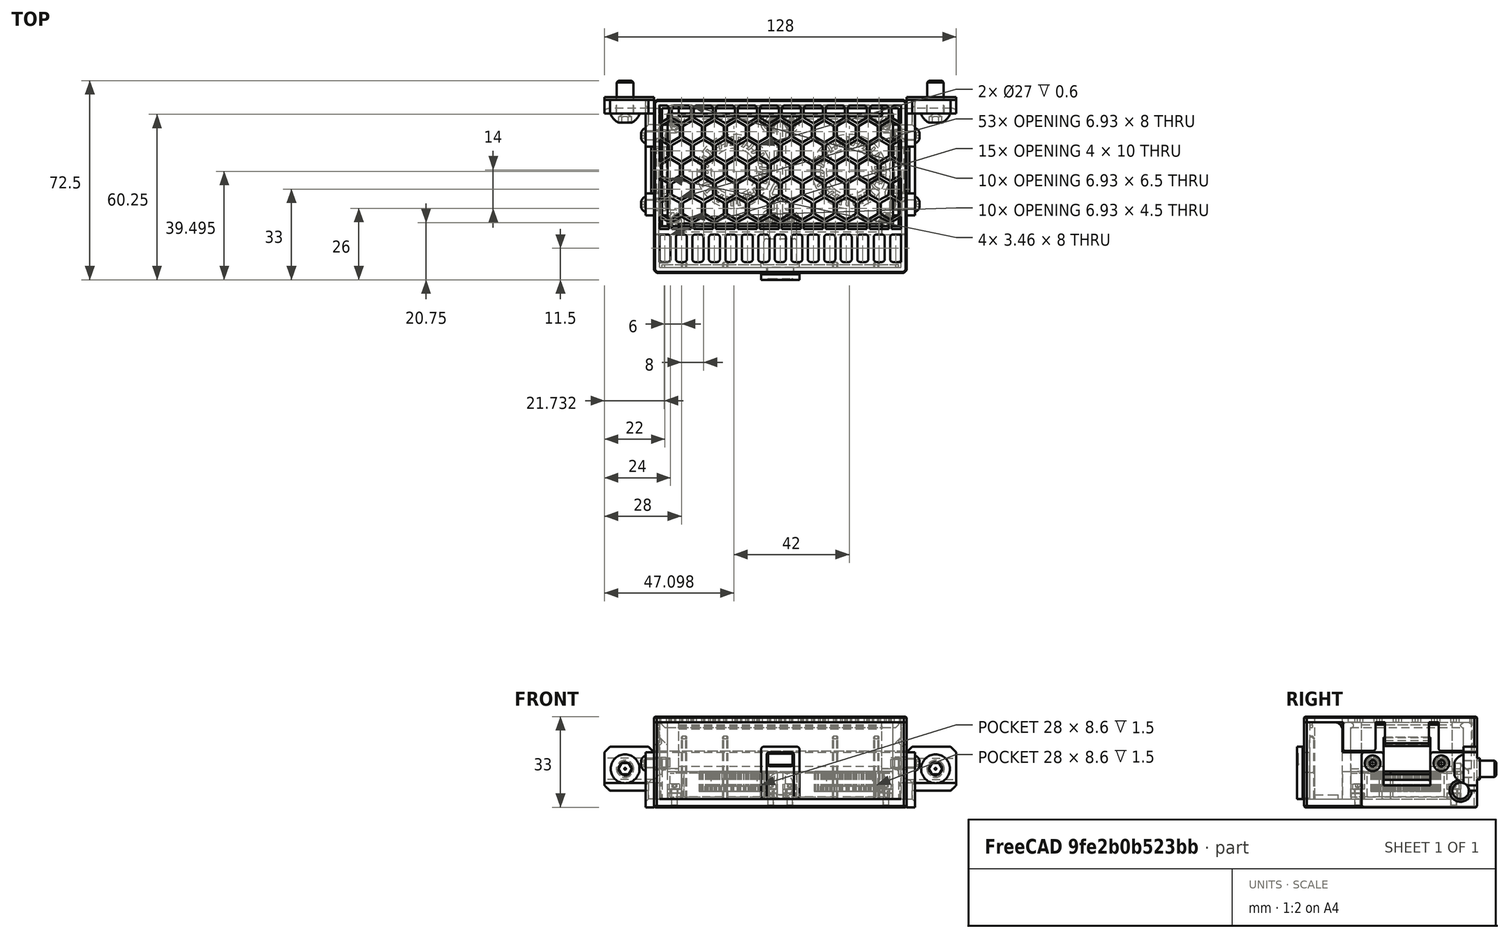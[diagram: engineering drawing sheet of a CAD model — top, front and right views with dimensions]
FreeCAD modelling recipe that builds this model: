
FCSTD DOCUMENT  (FreeCAD 0.19R24291 (Git))
Label: air-filter-assembly
License: Other
LicenseURL: GPL3
objects: Part::FeaturePython×18, Part::Feature×7, Part::Box×2, Spreadsheet::Sheet×2, PartDesign::CoordinateSystem×1, App::Part×1
note: 28 computed .brp shape members not serialized (recipe doc carries the construction recipe); baked Part::Feature solids carry a one-line shape summary decoded from their .brp

FEATURE [Part::Box] Box  label="hepa-filter"
  AttacherType = Attacher::AttachEngine3D
  Height = 16
  Length = 82
  Placement = pos=(-41,-20.5,13) rot=(0,0,1;0rad)
  Width = 41
FEATURE [Part::Box] Box001  label="active-carbon-foam"
  AttacherType = Attacher::AttachEngine3D
  Height = 28
  Length = 88
  Placement = pos=(-44,-33.5,3) rot=(0,0,1;0rad)
  Width = 10
FEATURE [Part::Feature] Part__Mirroring001001  label="air-filter-mounter-left"
  shape: bbox 18 x 43 x 22 mm, 33 faces (baked)
FEATURE [Part::Feature] Chamfer010015011016002001  label="air-filter-mounter-right"
  shape: bbox 18 x 43 x 22 mm, 33 faces (baked)
FEATURE [Part::Feature] Chamfer010015011013001001  label="air-filter-front-cover"
  shape: bbox 92 x 63 x 12.5 mm, 653 faces (baked)
FEATURE [Part::Feature] Chamfer010015011010001001  label="air-filter-body"
  shape: bbox 92 x 63 x 31 mm, 194 faces (baked)
FEATURE [Part::Feature] Cut019003010005001002001001  label="air-filter-eject-level"
  shape: bbox 14 x 15 x 19 mm, 37 faces (baked)
FEATURE [Part::Feature] Fusion036012039009  label="4010-fan001"
  Placement = pos=(-21.1,-20.5,3) rot=(-1,0,0;1.5708rad)
  shape: bbox 40 x 40 x 10 mm, 256 faces, 2 solids (baked)
FEATURE [Part::Feature] Fusion001021004009015013015  label="4010-fan002"
  Placement = pos=(20.9,-20.5,3) rot=(-1,0,0;1.5708rad)
  shape: bbox 40 x 40 x 10 mm, 256 faces, 2 solids (baked)
FEATURE [Part::FeaturePython] Screw  label="M3x6-Screw"  # Fasteners workbench fastener (typed FeaturePython)
  Placement = pos=(-49,12.5,16) rot=(0,-1,0;1.5708rad)
  baseObject = -> Part__Mirroring001001 [Edge89]
  diameter = 1
  invert = true
  length = 0
  lengthCustom = 6
  matchOuter = true
  offset = 0
  thread = false
  type = 39
FEATURE [Part::FeaturePython] Screw001  label="M3x6-Screw004"  # Fasteners workbench fastener (typed FeaturePython)
  Placement = pos=(-49,-12.5,16) rot=(0,-1,0;1.5708rad)
  baseObject = -> Part__Mirroring001001 [Edge91]
  diameter = 1
  invert = true
  length = 0
  lengthCustom = 6
  matchOuter = true
  offset = 0
  thread = false
  type = 39
FEATURE [Part::FeaturePython] Screw002  label="M3x6-Screw002"  # Fasteners workbench fastener (typed FeaturePython)
  Placement = pos=(49,12.5,16) rot=(0,1,0;1.5708rad)
  baseObject = -> Chamfer010015011016002001 [Edge89]
  diameter = 1
  invert = false
  length = 0
  lengthCustom = 6
  matchOuter = true
  offset = 0
  thread = false
  type = 39
FEATURE [Part::FeaturePython] Screw003  label="M3x6-Screw003"  # Fasteners workbench fastener (typed FeaturePython)
  Placement = pos=(49,-12.5,16) rot=(0,1,0;1.5708rad)
  baseObject = -> Chamfer010015011016002001 [Edge91]
  diameter = 1
  invert = false
  length = 0
  lengthCustom = 6
  matchOuter = true
  offset = 0
  thread = false
  type = 39
FEATURE [Part::FeaturePython] Screw004  label="M6x12-Screw"  # Fasteners workbench fastener (typed FeaturePython)
  Placement = pos=(-56.5,20.5,14) rot=(1,0,0;1.5708rad)
  baseObject = -> Part__Mirroring001001 [Edge57]
  diameter = 4
  invert = false
  length = 1
  lengthCustom = 12
  matchOuter = true
  offset = 0
  thread = false
  type = 39
FEATURE [Part::FeaturePython] Screw005  label="M6x12-Screw001"  # Fasteners workbench fastener (typed FeaturePython)
  Placement = pos=(56.5,20.5,14) rot=(1,0,0;1.5708rad)
  baseObject = -> Chamfer010015011016002001 [Edge40]
  diameter = 4
  invert = true
  length = 1
  lengthCustom = 12
  matchOuter = true
  offset = 0
  thread = false
  type = 39
FEATURE [Part::FeaturePython] HeatSet  label="M3x3-HeatSet003"  # WARN: FeaturePython — macro-defined, semantics opaque (R4)
  Placement = pos=(-46,12.5,16) rot=(0,-1,0;1.5708rad)
  baseObject = -> Chamfer010015011010001001 [Edge17]
  diameter = 2
  invert = true
  offset = 0
FEATURE [Part::FeaturePython] HeatSet001  label="M3x3-HeatSet001"  # WARN: FeaturePython — macro-defined, semantics opaque (R4)
  Placement = pos=(-46,-12.5,16) rot=(0,-1,0;1.5708rad)
  baseObject = -> Chamfer010015011010001001 [Edge16]
  diameter = 2
  invert = true
  offset = 0
FEATURE [Part::FeaturePython] HeatSet002  label="M3x3-HeatSet"  # WARN: FeaturePython — macro-defined, semantics opaque (R4)
  Placement = pos=(46,12.5,16) rot=(0,1,0;1.5708rad)
  baseObject = -> Chamfer010015011010001001 [Edge138]
  diameter = 2
  invert = false
  offset = 0
FEATURE [Part::FeaturePython] HeatSet003  label="M3x3-HeatSet002"  # WARN: FeaturePython — macro-defined, semantics opaque (R4)
  Placement = pos=(46,-12.5,16) rot=(0,1,0;1.5708rad)
  baseObject = -> Chamfer010015011010001001 [Edge137]
  diameter = 2
  invert = false
  offset = 0
FEATURE [Part::FeaturePython] Screw006  label="M2x6-self-tapping-Screw"  # Fasteners workbench fastener (typed FeaturePython)
  Placement = pos=(-38.6016,16.9954,6.499) rot=(0,0,1;0rad)
  baseObject = -> Fusion036012039009 [Edge191]
  diameter = 2
  invert = true
  length = 3
  lengthCustom = 6
  matchOuter = true
  offset = 0
  thread = false
  type = 34
FEATURE [Part::FeaturePython] Screw007  label="M2x6-self-tapping-Screw001"  # Fasteners workbench fastener (typed FeaturePython)
  Placement = pos=(-38.6016,-18.0046,6.499) rot=(0,0,1;0rad)
  baseObject = -> Fusion036012039009 [Edge1]
  diameter = 2
  invert = true
  length = 3
  lengthCustom = 6
  matchOuter = true
  offset = 0
  thread = false
  type = 34
FEATURE [Part::FeaturePython] Screw008  label="M2x6-self-tapping-Screw002"  # Fasteners workbench fastener (typed FeaturePython)
  Placement = pos=(-3.60162,16.9954,6.499) rot=(0,0,1;0rad)
  baseObject = -> Fusion036012039009 [Edge4]
  diameter = 2
  invert = true
  length = 3
  lengthCustom = 6
  matchOuter = true
  offset = 0
  thread = false
  type = 34
FEATURE [Part::FeaturePython] Screw009  label="M2x6-self-tapping-Screw003"  # Fasteners workbench fastener (typed FeaturePython)
  Placement = pos=(-3.60162,-18.0046,6.499) rot=(0,0,1;0rad)
  baseObject = -> Fusion036012039009 [Edge197]
  diameter = 2
  invert = true
  length = 3
  lengthCustom = 6
  matchOuter = true
  offset = 0
  thread = false
  type = 34
FEATURE [Part::FeaturePython] Screw010  label="M2x6-self-tapping-Screw004"  # Fasteners workbench fastener (typed FeaturePython)
  Placement = pos=(3.39838,-18.0046,6.499) rot=(0,0,1;0rad)
  baseObject = -> Fusion001021004009015013015 [Edge1]
  diameter = 2
  invert = true
  length = 3
  lengthCustom = 6
  matchOuter = true
  offset = 0
  thread = false
  type = 34
FEATURE [Part::FeaturePython] Screw011  label="M2x6-self-tapping-Screw005"  # Fasteners workbench fastener (typed FeaturePython)
  Placement = pos=(3.39838,16.9954,6.499) rot=(0,0,1;0rad)
  baseObject = -> Fusion001021004009015013015 [Edge190]
  diameter = 2
  invert = true
  length = 3
  lengthCustom = 6
  matchOuter = true
  offset = 0
  thread = false
  type = 34
FEATURE [Part::FeaturePython] Screw012  label="M2x6-self-tapping-Screw006"  # Fasteners workbench fastener (typed FeaturePython)
  Placement = pos=(38.3984,16.9954,6.499) rot=(0,0,1;0rad)
  baseObject = -> Fusion001021004009015013015 [Edge4]
  diameter = 2
  invert = true
  length = 3
  lengthCustom = 6
  matchOuter = true
  offset = 0
  thread = false
  type = 34
FEATURE [Part::FeaturePython] Screw013  label="M2x6-self-tapping-Screw007"  # Fasteners workbench fastener (typed FeaturePython)
  Placement = pos=(38.3984,-18.0046,6.499) rot=(0,0,1;0rad)
  baseObject = -> Fusion001021004009015013015 [Edge196]
  diameter = 2
  invert = true
  length = 3
  lengthCustom = 6
  matchOuter = true
  offset = 0
  thread = false
  type = 34
FEATURE [PartDesign::CoordinateSystem] LCS_air_filter  label="LCS_air-filter"
  AttacherType = Attacher::AttachEngine3D
FEATURE [App::Part] Part  label="air-filter"
  Group = -> [Box001,Box,Screw,Screw004,Screw001,Part__Mirroring001001,Screw005,Screw002,Screw003,Chamfer010015011016002001,Chamfer010015011013001001,Chamfer010015011010001001,Cut019003010005001002001001,Fusion036012039009,Fusion001021004009015013015,HeatSet002,HeatSet001,HeatSet003,HeatSet,Screw006,Screw007,Screw008,Screw009,Screw010,Screw011,Screw012,Screw013,LCS_air_filter]
  Origin = -> Origin
FEATURE [Spreadsheet::Sheet] Fasteners_BOM
  cells = A1=Type; B1=Qty; A2=Heat Set Insert M3; B2=8; A3=ISO4762 Screw M2x6; B3=16; A4=ISO7380-1 Screw M3x6; B4=8; A5=ISO7380-1 Screw M6x12; B5=4
FEATURE [Spreadsheet::Sheet] Fasteners_BOM001
  cells = A1=Type; B1=Qty; A2=Heat Set Insert M3; B2=8; A3=ISO4762 Screw M2x6; B3=16; A4=ISO7380-1 Screw M3x6; B4=8; A5=ISO7380-1 Screw M6x12; B5=4
